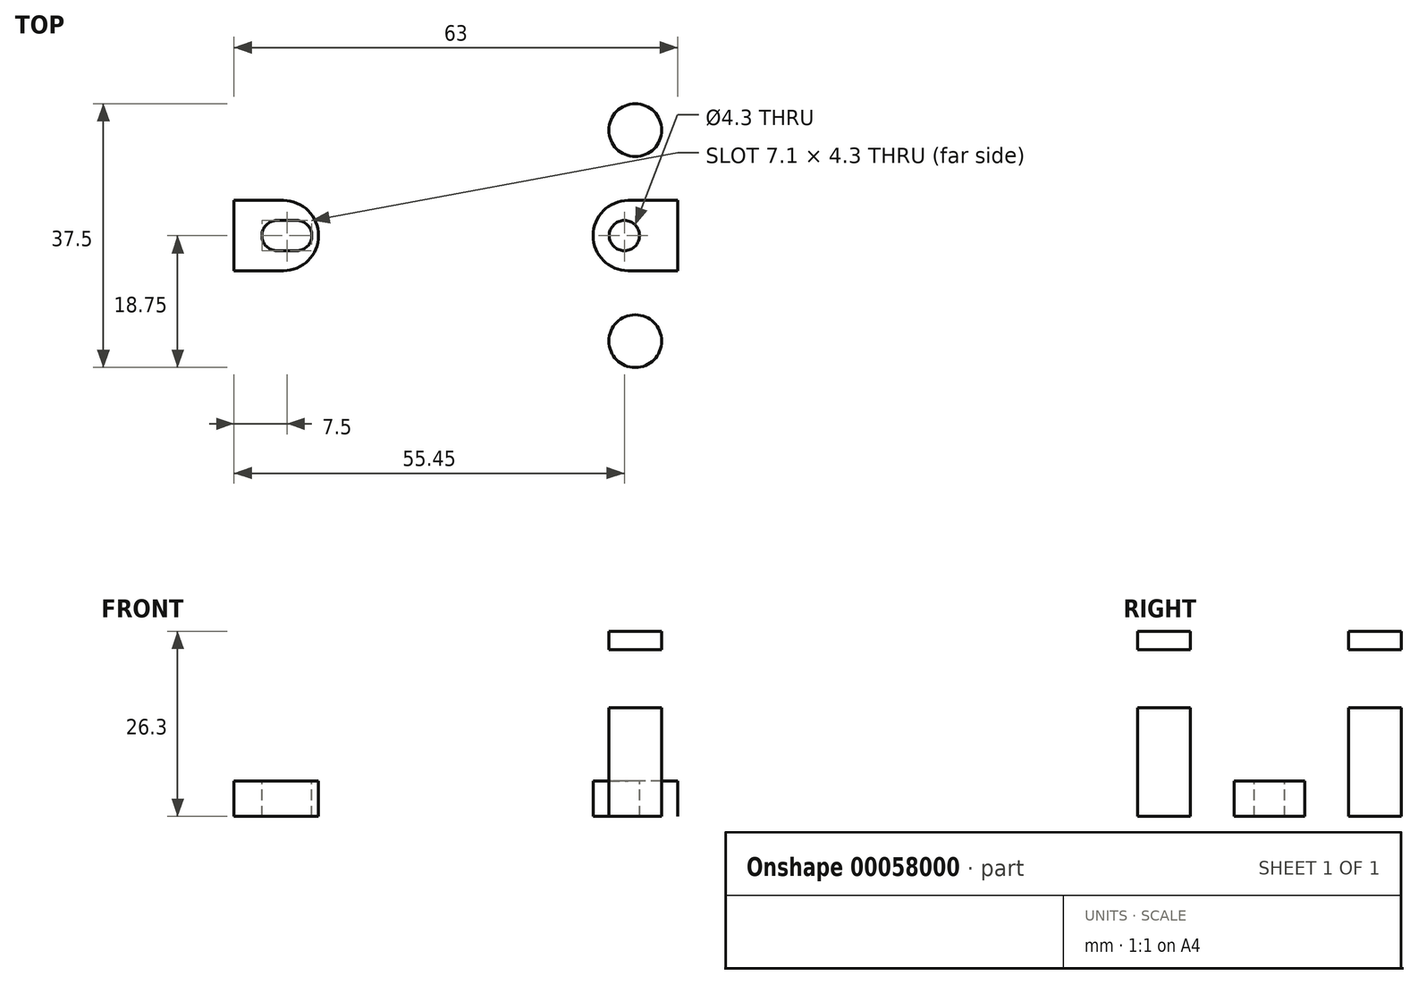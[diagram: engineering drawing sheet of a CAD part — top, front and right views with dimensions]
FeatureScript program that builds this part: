
annotation { "Feature Type Name" : "Feature", "Feature Type Description" : "" }
export const myFeature = defineFeature(function(context is Context, id is Id, definition is map)
    precondition{}
    {
        {
            var Q0;
            Q0=qCreatedBy(makeId("Top.planeOp"),FACE);
            var sketch = newSketch(context, id + "F0", { "sketchPlane" : qUnion([Q0])});
            skLineSegment(sketch, "E0.bottom", {"start": v(0, 0) * mm, "end": v(63, 0) * mm});
            skLineSegment(sketch, "E0.top", {"start": v(0, 46) * mm, "end": v(63, 46) * mm});
            skLineSegment(sketch, "E0.left", {"start": v(0, 0) * mm, "end": v(0, 46) * mm});
            skLineSegment(sketch, "E0.right", {"start": v(63, 0) * mm, "end": v(63, 46) * mm});
            skSolve(sketch);
        }
        {
            var Q0;
            Q0=makeQuery(id+"F0.imprint","IMPRINT",FACE,{"disambiguationData":[TD([[makeQuery(id+"F0.imprint","IMPRINT",EDGE,{"derivedFrom":sQuery(id+"F0.wireOp",EDGE,"E0.bottom")}),1.0]])]});
            extrude(context, id + "F1", {"entities" : qUnion([Q0]), "depth" : 26.3 * mm});
        }
        {
            var Q0;
            Q0=makeQuery(id+"F1.opExtrude","CAP_FACE",FACE,{"disambiguationData":[OSD([sQuery(id+"F0.wireOp",EDGE,"E0.bottom"),sQuery(id+"F0.wireOp",EDGE,"E0.top"),sQuery(id+"F0.wireOp",EDGE,"E0.left"),sQuery(id+"F0.wireOp",EDGE,"E0.right")])],"isStart":false});
            var sketch = newSketch(context, id + "F2", { "sketchPlane" : qUnion([Q0])});
            skLineSegment(sketch, "E1.bottom", {"start": v(0, 28) * mm, "end": v(7, 28) * mm});
            skLineSegment(sketch, "E1.top", {"start": v(0, 18) * mm, "end": v(7, 18) * mm});
            skLineSegment(sketch, "E1.left", {"start": v(0, 28) * mm, "end": v(0, 18) * mm});
            skLineSegment(sketch, "E2", {"start": v(31.5, 46) * mm, "end": v(31.5, 23) * mm, "construction": true});
            skLineSegment(sketch, "E3", {"start": v(31.5, 23) * mm, "end": v(31.5, 0) * mm, "construction": true});
            skArc(sketch, "E4", {"start": v(7, 18) * mm, "mid": v(12, 23) * mm, "end": v(7, 28) * mm});
            skLineSegment(sketch, "E5.MirrorCS", {"start": v(63, 28) * mm, "end": v(56, 28) * mm});
            skArc(sketch, "E6.MirrorCS", {"start": v(56, 18) * mm, "mid": v(51, 23) * mm, "end": v(56, 28) * mm});
            skLineSegment(sketch, "E7.MirrorCS", {"start": v(63, 18) * mm, "end": v(56, 18) * mm});
            skLineSegment(sketch, "E8.MirrorCS", {"start": v(63, 28) * mm, "end": v(63, 18) * mm});
            skLineSegment(sketch, "E9", {"start": v(31.5, 23) * mm, "end": v(7, 23) * mm, "construction": true});
            skSolve(sketch);
        }
        {
            var Q0;
            Q0=makeQuery(id+"F2.imprint","IMPRINT",FACE,{"disambiguationData":[TD([[makeQuery(id+"F2.imprint","IMPRINT",EDGE,{"derivedFrom":sQuery(id+"F2.wireOp",EDGE,"E1.bottom")}),-1.0]])]});
            var Q1;
            Q1=makeQuery(id+"F2.imprint","IMPRINT",FACE,{"disambiguationData":[TD([[makeQuery(id+"F2.imprint","IMPRINT",EDGE,{"derivedFrom":sQuery(id+"F2.wireOp",EDGE,"E5.MirrorCS")}),1.0]])]});
            extrude(context, id + "F3", {"entities" : qUnion([Q0, Q1]), "operationType" : NewBodyOperationType.REMOVE, "oppositeDirection" : true, "depth" : 21.3 * mm});
        }
        {
            var Q0;
            Q0=makeQuery(id+"F3.boolean.opBoolean","COPY",FACE,{"derivedFrom":makeQuery(id+"F3.opExtrude","CAP_FACE",FACE,{"disambiguationData":[OSD([sQuery(id+"F2.wireOp",EDGE,"E1.bottom"),sQuery(id+"F2.wireOp",EDGE,"E1.top"),sQuery(id+"F2.wireOp",EDGE,"E1.left"),sQuery(id+"F2.wireOp",EDGE,"E4")])],"isStart":false})});
            var sketch = newSketch(context, id + "F4", { "sketchPlane" : qUnion([Q0])});
            skLineSegment(sketch, "E10", {"start": v(0, 23) * mm, "end": v(4, 23) * mm, "construction": true});
            skLineSegment(sketch, "E11.bottom", {"start": v(6.1, 25.15) * mm, "end": v(8.9, 25.15) * mm});
            skLineSegment(sketch, "E11.top", {"start": v(6.1, 20.85) * mm, "end": v(8.9, 20.85) * mm});
            skLineSegment(sketch, "E12", {"start": v(4, 23) * mm, "end": v(6.1, 23) * mm, "construction": true});
            skLineSegment(sketch, "E13", {"start": v(6.1, 23) * mm, "end": v(8.9, 23) * mm, "construction": true});
            skLineSegment(sketch, "E14", {"start": v(8.9, 23) * mm, "end": v(11, 23) * mm, "construction": true});
            skArc(sketch, "E15", {"start": v(6.1, 25.15) * mm, "mid": v(3.95, 23) * mm, "end": v(6.1, 20.85) * mm});
            skArc(sketch, "E16", {"start": v(8.9, 20.85) * mm, "mid": v(11.05, 23) * mm, "end": v(8.9, 25.15) * mm});
            skPoint(sketch, "E17.orphan", {"position": v(11, 25.15) * mm});
            skPoint(sketch, "E18.orphan", {"position": v(11, 20.85) * mm});
            skPoint(sketch, "E11.left.end.orphan", {"position": v(4, 20.85) * mm});
            skPoint(sketch, "E19.orphan", {"position": v(4, 25.15) * mm});
            skLineSegment(sketch, "E20", {"start": v(11, 23) * mm, "end": v(55.45, 23) * mm, "construction": true});
            skCircle(sketch, "E21", {"center": v(55.45, 23) * mm, "radius": 2.15 * mm});
            skLineSegment(sketch, "E22", {"start": v(57.6, 22.9) * mm, "end": v(63, 22.9) * mm, "construction": true});
            skSolve(sketch);
        }
        {
            var Q0;
            Q0=makeQuery(id+"F4.imprint","IMPRINT",FACE,{"disambiguationData":[TD([[makeQuery(id+"F4.imprint","IMPRINT",EDGE,{"derivedFrom":sQuery(id+"F4.wireOp",EDGE,"E11.bottom")}),-1.0]])]});
            var Q1;
            Q1=makeQuery(id+"F4.imprint","IMPRINT",FACE,{"disambiguationData":[TD([[makeQuery(id+"F4.imprint","IMPRINT",EDGE,{"derivedFrom":sQuery(id+"F4.wireOp",EDGE,"E21")}),1.0]])]});
            extrude(context, id + "F5", {"entities" : qUnion([Q0, Q1]), "operationType" : NewBodyOperationType.REMOVE, "endBound" : BoundingType.THROUGH_ALL, "oppositeDirection" : true, "depth" : 25 * mm});
        }
        {
            var Q0;
            Q0=makeQuery(id+"F1.opExtrude","SWEPT_FACE",FACE,{"disambiguationData":[OSD([sQuery(id+"F0.wireOp",EDGE,"E0.right")])]});
            var sketch = newSketch(context, id + "F6", { "sketchPlane" : qUnion([Q0])});
            skLineSegment(sketch, "E23.bottom", {"start": v(2.35, 23.7) * mm, "end": v(15.1, 23.7) * mm});
            skLineSegment(sketch, "E23.top", {"start": v(2.35, 15.45) * mm, "end": v(15.1, 15.45) * mm});
            skLineSegment(sketch, "E23.left", {"start": v(2.35, 23.7) * mm, "end": v(2.35, 15.45) * mm});
            skLineSegment(sketch, "E23.right", {"start": v(15.1, 23.7) * mm, "end": v(15.1, 15.45) * mm});
            skLineSegment(sketch, "E24.bottom", {"start": v(30.9, 23.7) * mm, "end": v(43.65, 23.7) * mm});
            skLineSegment(sketch, "E24.top", {"start": v(30.9, 15.45) * mm, "end": v(43.65, 15.45) * mm});
            skLineSegment(sketch, "E24.left", {"start": v(30.9, 23.7) * mm, "end": v(30.9, 15.45) * mm});
            skLineSegment(sketch, "E24.right", {"start": v(43.65, 23.7) * mm, "end": v(43.65, 15.45) * mm});
            skLineSegment(sketch, "E25", {"start": v(0, 6.87) * mm, "end": v(23, 6.87) * mm, "construction": true});
            skPoint(sketch, "E25.endSnap0", {"position": v(23, 5) * mm});
            skLineSegment(sketch, "E26", {"start": v(23, 6.87) * mm, "end": v(46, 6.87) * mm, "construction": true});
            skLineSegment(sketch, "E27", {"start": v(15.1, 15.45) * mm, "end": v(23, 15.45) * mm, "construction": true});
            skLineSegment(sketch, "E28", {"start": v(23, 15.45) * mm, "end": v(30.9, 15.45) * mm, "construction": true});
            skLineSegment(sketch, "E29", {"start": v(2.35, 15.45) * mm, "end": v(0, 15.45) * mm, "construction": true});
            skLineSegment(sketch, "E30", {"start": v(2.35, 23.7) * mm, "end": v(2.35, 26.3) * mm, "construction": true});
            skSolve(sketch);
        }
        {
            var Q0;
            Q0=makeQuery(id+"F6.imprint","IMPRINT",FACE,{"disambiguationData":[TD([[makeQuery(id+"F6.imprint","IMPRINT",EDGE,{"derivedFrom":sQuery(id+"F6.wireOp",EDGE,"E24.bottom")}),-1.0]])]});
            var Q1;
            Q1=makeQuery(id+"F6.imprint","IMPRINT",FACE,{"disambiguationData":[TD([[makeQuery(id+"F6.imprint","IMPRINT",EDGE,{"derivedFrom":sQuery(id+"F6.wireOp",EDGE,"E23.bottom")}),-1.0]])]});
            extrude(context, id + "F7", {"entities" : qUnion([Q0, Q1]), "operationType" : NewBodyOperationType.REMOVE, "endBound" : BoundingType.THROUGH_ALL, "oppositeDirection" : true, "depth" : 12.5 * mm});
        }
        {
            var Q0;
            Q0=qCreatedBy(makeId("Top.planeOp"),FACE);
            var sketch = newSketch(context, id + "F8", { "sketchPlane" : qUnion([Q0])});
            skLineSegment(sketch, "E31.bottom", {"start": v(12.5, 0) * mm, "end": v(50.5, 0) * mm});
            skLineSegment(sketch, "E31.top", {"start": v(12.5, 46) * mm, "end": v(50.5, 46) * mm});
            skLineSegment(sketch, "E31.left", {"start": v(12.5, 0) * mm, "end": v(12.5, 46) * mm});
            skLineSegment(sketch, "E31.right", {"start": v(50.5, 0) * mm, "end": v(50.5, 46) * mm});
            skLineSegment(sketch, "E32", {"start": v(12.5, 0) * mm, "end": v(0, 0) * mm, "construction": true});
            skSolve(sketch);
        }
        {
            var Q0;
            Q0 = qSketchRegion(id + "F8", true);
            var Q1;
            Q1=makeQuery(id+"F1.opExtrude","CAP_FACE",FACE,{"disambiguationData":[OSD([sQuery(id+"F0.wireOp",EDGE,"E0.bottom"),sQuery(id+"F0.wireOp",EDGE,"E0.top"),sQuery(id+"F0.wireOp",EDGE,"E0.left"),sQuery(id+"F0.wireOp",EDGE,"E0.right")])],"isStart":false});
            extrude(context, id + "F9", {"entities" : qUnion([Q0]), "operationType" : NewBodyOperationType.ADD, "endBound" : BoundingType.UP_TO_SURFACE, "endBoundEntityFace" : qUnion([Q1]), "depth" : 25 * mm});
        }
        {
            var Q0;
            Q0=makeQuery(id+"F1.opExtrude","CAP_FACE",FACE,{"disambiguationData":[OSD([sQuery(id+"F0.wireOp",EDGE,"E0.bottom"),sQuery(id+"F0.wireOp",EDGE,"E0.top"),sQuery(id+"F0.wireOp",EDGE,"E0.left"),sQuery(id+"F0.wireOp",EDGE,"E0.right")])],"isStart":false});
            var sketch = newSketch(context, id + "F10", { "sketchPlane" : qUnion([Q0])});
            skLineSegment(sketch, "E33", {"start": v(6, 0) * mm, "end": v(6, 8) * mm, "construction": true});
            skLineSegment(sketch, "E34", {"start": v(6, 8) * mm, "end": v(0, 8) * mm, "construction": true});
            skLineSegment(sketch, "E35", {"start": v(0, 38) * mm, "end": v(6, 38) * mm, "construction": true});
            skLineSegment(sketch, "E36", {"start": v(6, 38) * mm, "end": v(6, 46) * mm, "construction": true});
            skCircle(sketch, "E37", {"center": v(6, 38) * mm, "radius": 3.75 * mm});
            skCircle(sketch, "E38", {"center": v(6, 8) * mm, "radius": 3.75 * mm});
            skLineSegment(sketch, "E39", {"start": v(31.5, 46) * mm, "end": v(31.5, 0) * mm, "construction": true});
            skCircle(sketch, "E40.MirrorC", {"center": v(57, 8) * mm, "radius": 3.75 * mm});
            skCircle(sketch, "E41.MirrorC", {"center": v(57, 38) * mm, "radius": 3.75 * mm});
            skSolve(sketch);
        }
        {
            var Q0;
            Q0=makeQuery(id+"F10.imprint","IMPRINT",FACE,{"disambiguationData":[TD([[makeQuery(id+"F10.imprint","IMPRINT",EDGE,{"derivedFrom":sQuery(id+"F10.wireOp",EDGE,"E37")}),1.0]])]});
            var Q1;
            Q1=makeQuery(id+"F10.imprint","IMPRINT",FACE,{"disambiguationData":[TD([[makeQuery(id+"F10.imprint","IMPRINT",EDGE,{"derivedFrom":sQuery(id+"F10.wireOp",EDGE,"E38")}),1.0]])]});
            var Q2;
            Q2=makeQuery(id+"F10.imprint","IMPRINT",FACE,{"disambiguationData":[TD([[makeQuery(id+"F10.imprint","IMPRINT",EDGE,{"derivedFrom":sQuery(id+"F10.wireOp",EDGE,"E41.MirrorC")}),-1.0]])]});
            var Q3;
            Q3=makeQuery(id+"F10.imprint","IMPRINT",FACE,{"disambiguationData":[TD([[makeQuery(id+"F10.imprint","IMPRINT",EDGE,{"derivedFrom":sQuery(id+"F10.wireOp",EDGE,"E40.MirrorC")}),-1.0]])]});
            extrude(context, id + "F11", {"entities" : qUnion([Q0, Q1, Q2, Q3]), "operationType" : NewBodyOperationType.REMOVE, "endBound" : BoundingType.UP_TO_NEXT, "oppositeDirection" : true, "depth" : 25 * mm});
        }
    });
